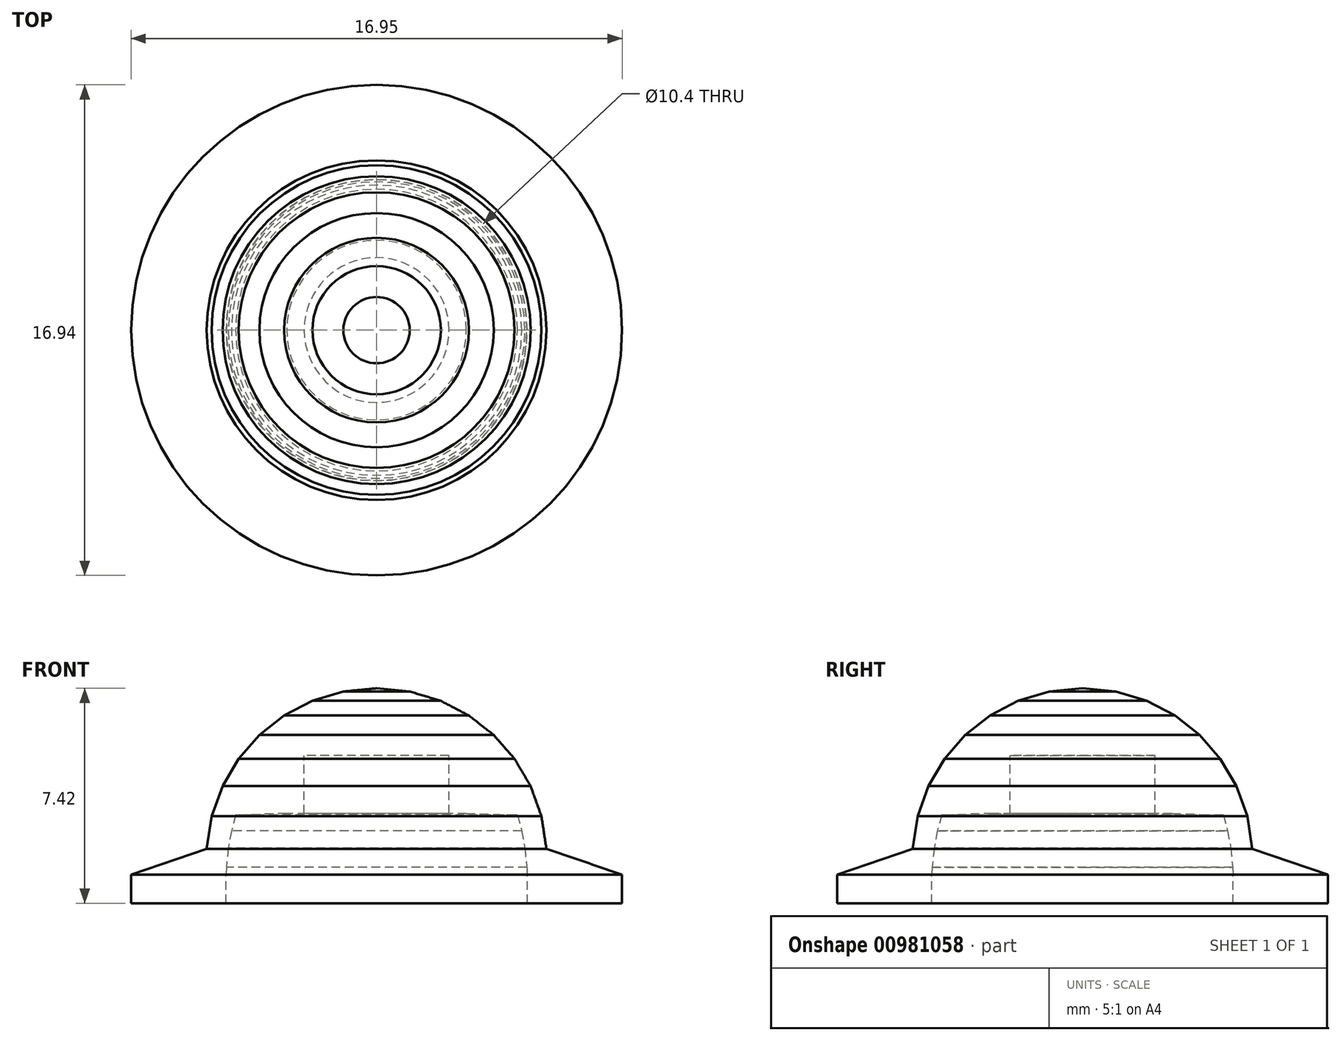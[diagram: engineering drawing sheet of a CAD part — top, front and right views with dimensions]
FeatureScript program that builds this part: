
annotation { "Feature Type Name" : "Feature", "Feature Type Description" : "" }
export const myFeature = defineFeature(function(context is Context, id is Id, definition is map)
    precondition{}
    {
        {
            var Q0;
            Q0=qCreatedBy(makeId("Front.planeOp"),FACE);
            var sketch = newSketch(context, id + "F0", { "sketchPlane" : qUnion([Q0])});
            skLineSegment(sketch, "E0", {"start": v(4.24, -3.71) * mm, "end": v(4.24, -2.72) * mm});
            skLineSegment(sketch, "E1", {"start": v(4.24, -2.72) * mm, "end": v(1.63, -1.84) * mm});
            skLineSegment(sketch, "E2", {"start": v(1.63, -1.84) * mm, "end": v(1.63, -1.83) * mm});
            skLineSegment(sketch, "E3", {"start": v(1.63, -1.83) * mm, "end": v(1.46, -0.7) * mm});
            skLineSegment(sketch, "E4", {"start": v(1.46, -0.7) * mm, "end": v(1.08, 0.34) * mm});
            skLineSegment(sketch, "E5", {"start": v(1.08, 0.34) * mm, "end": v(0.52, 1.28) * mm});
            skLineSegment(sketch, "E6", {"start": v(0.52, 1.28) * mm, "end": v(-0.2, 2.1) * mm});
            skLineSegment(sketch, "E7", {"start": v(-0.2, 2.1) * mm, "end": v(-1.05, 2.77) * mm});
            skLineSegment(sketch, "E8", {"start": v(-1.05, 2.77) * mm, "end": v(-2.02, 3.28) * mm});
            skLineSegment(sketch, "E9", {"start": v(-2.02, 3.28) * mm, "end": v(-3.1, 3.6) * mm});
            skLineSegment(sketch, "E10", {"start": v(-3.1, 3.6) * mm, "end": v(-4.24, 3.71) * mm});
            skLineSegment(sketch, "E11", {"start": v(-4.24, 3.71) * mm, "end": v(-4.24, 1.39) * mm});
            skLineSegment(sketch, "E12", {"start": v(-4.24, 1.39) * mm, "end": v(-1.74, 1.39) * mm});
            skLineSegment(sketch, "E13", {"start": v(-1.74, 1.39) * mm, "end": v(-1.74, -0.61) * mm});
            skLineSegment(sketch, "E14", {"start": v(-1.74, -0.61) * mm, "end": v(-1.14, -0.61) * mm});
            skLineSegment(sketch, "E15", {"start": v(-1.14, -0.61) * mm, "end": v(-1.14, 1.12) * mm});
            skLineSegment(sketch, "E16", {"start": v(-1.14, 1.12) * mm, "end": v(-1.12, 1.2) * mm});
            skLineSegment(sketch, "E17", {"start": v(-1.12, 1.2) * mm, "end": v(-1.09, 1.29) * mm});
            skLineSegment(sketch, "E18", {"start": v(-1.09, 1.29) * mm, "end": v(-1.03, 1.35) * mm});
            skLineSegment(sketch, "E19", {"start": v(-1.03, 1.35) * mm, "end": v(-0.95, 1.4) * mm});
            skLineSegment(sketch, "E20", {"start": v(-0.95, 1.4) * mm, "end": v(-0.87, 1.42) * mm});
            skLineSegment(sketch, "E21", {"start": v(-0.87, 1.42) * mm, "end": v(-0.78, 1.42) * mm});
            skLineSegment(sketch, "E22", {"start": v(-0.78, 1.42) * mm, "end": v(-0.7, 1.4) * mm});
            skLineSegment(sketch, "E23", {"start": v(-0.7, 1.4) * mm, "end": v(-0.63, 1.34) * mm});
            skLineSegment(sketch, "E24", {"start": v(-0.63, 1.34) * mm, "end": v(-0.31, 1.01) * mm});
            skLineSegment(sketch, "E25", {"start": v(-0.31, 1.01) * mm, "end": v(-0.03, 0.66) * mm});
            skLineSegment(sketch, "E26", {"start": v(-0.03, 0.66) * mm, "end": v(0.22, 0.26) * mm});
            skLineSegment(sketch, "E27", {"start": v(0.22, 0.26) * mm, "end": v(0.44, -0.18) * mm});
            skLineSegment(sketch, "E28", {"start": v(0.44, -0.18) * mm, "end": v(0.63, -0.67) * mm});
            skLineSegment(sketch, "E29", {"start": v(0.63, -0.67) * mm, "end": v(0.77, -1.2) * mm});
            skLineSegment(sketch, "E30", {"start": v(0.77, -1.2) * mm, "end": v(0.88, -1.8) * mm});
            skLineSegment(sketch, "E31", {"start": v(0.88, -1.8) * mm, "end": v(0.95, -2.47) * mm});
            skLineSegment(sketch, "E32", {"start": v(0.95, -2.47) * mm, "end": v(0.96, -2.71) * mm});
            skLineSegment(sketch, "E33", {"start": v(0.96, -2.71) * mm, "end": v(0.96, -3.71) * mm});
            skLineSegment(sketch, "E34", {"start": v(0.96, -3.71) * mm, "end": v(4.24, -3.71) * mm});
            skLineSegment(sketch, "E35", {"start": v(-1.14, -0.61) * mm, "end": v(0.63, -0.67) * mm});
            skSolve(sketch);
        }
        {
            var Q0;
            Q0=makeQuery(id+"F0.imprint","IMPRINT",FACE,{"disambiguationData":[TD([[makeQuery(id+"F0.imprint","IMPRINT",EDGE,{"derivedFrom":sQuery(id+"F0.wireOp",EDGE,"E0")}),1.0]])]});
            var Q1;
            Q1=makeQuery(id+"F0.imprint","IMPRINT",FACE,{"disambiguationData":[TD([[makeQuery(id+"F0.imprint","IMPRINT",EDGE,{"derivedFrom":sQuery(id+"F0.wireOp",EDGE,"E15")}),-1.0]])]});
            var Q2;
            Q2=sQuery(id+"F0.wireOp",EDGE,"E11");
            revolve(context, id + "F1", {"surfaceOperationType" : NewSurfaceOperationType.NEW, "entities" : qUnion([Q0, Q1]), "axis" : qUnion([Q2]), "revolveType" : RevolveType.FULL});
        }
    });
